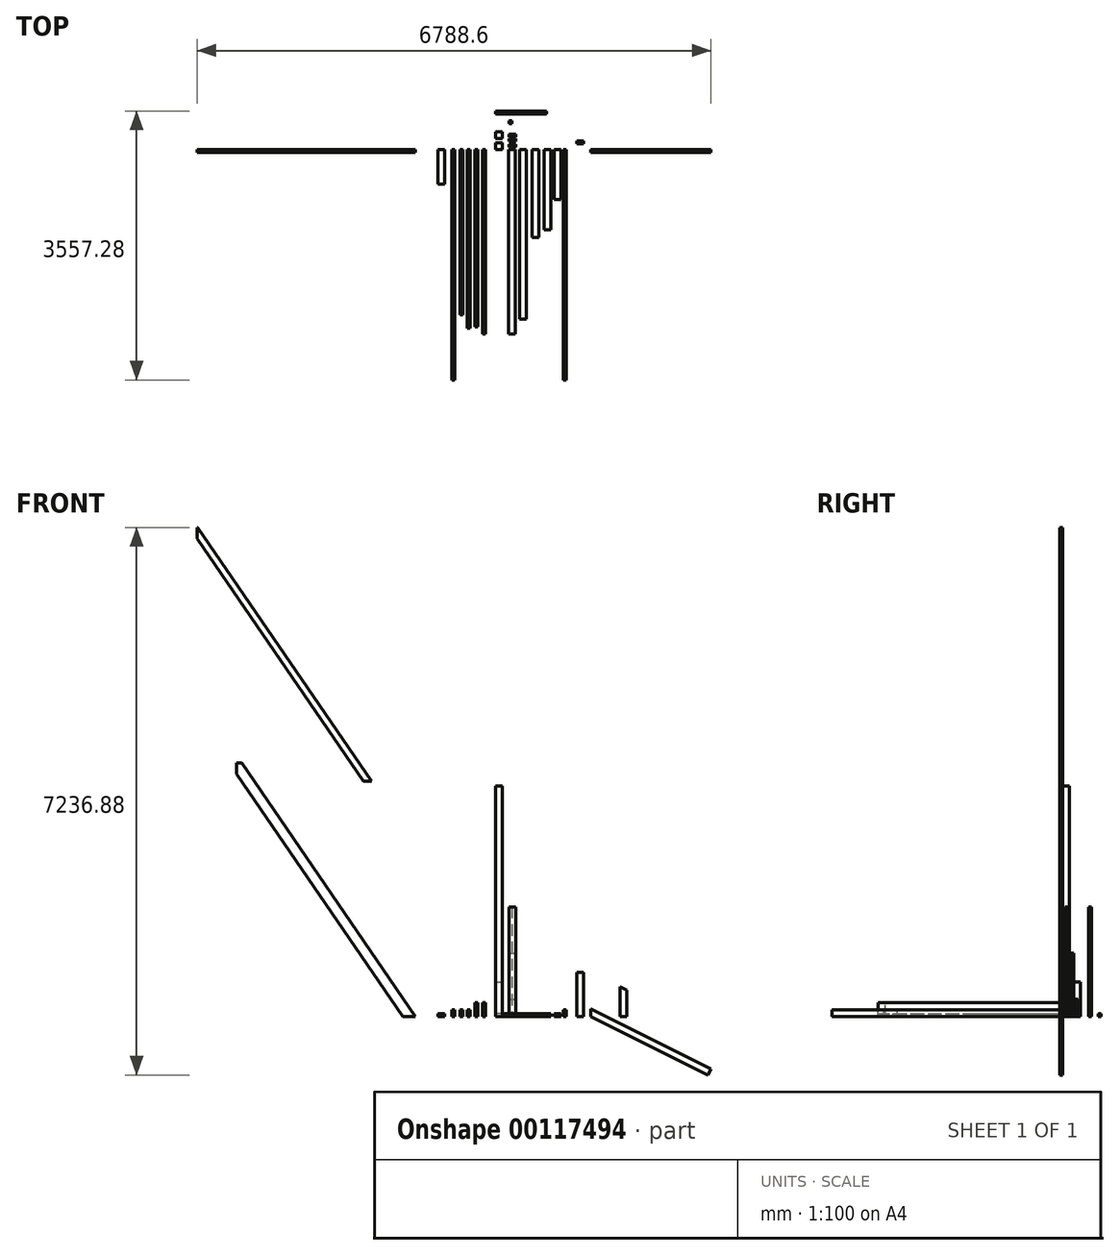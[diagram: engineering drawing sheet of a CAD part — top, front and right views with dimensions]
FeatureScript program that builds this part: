
annotation { "Feature Type Name" : "Feature", "Feature Type Description" : "" }
export const myFeature = defineFeature(function(context is Context, id is Id, definition is map)
    precondition{}
    {
        {
            var Q0;
            Q0=qCreatedBy(makeId("Top.planeOp"),FACE);
            var sketch = newSketch(context, id + "F0", { "sketchPlane" : qUnion([Q0])});
            skLineSegment(sketch, "E0.bottom", {"start": v(0, 0) * mm, "end": v(88.9, 0) * mm});
            skLineSegment(sketch, "E0.top", {"start": v(0, 88.9) * mm, "end": v(88.9, 88.9) * mm});
            skLineSegment(sketch, "E0.left", {"start": v(0, 0) * mm, "end": v(0, 88.9) * mm});
            skLineSegment(sketch, "E0.right", {"start": v(88.9, 0) * mm, "end": v(88.9, 88.9) * mm});
            skSolve(sketch);
        }
        {
            var Q0;
            Q0=makeQuery(id+"F0.imprint","IMPRINT",FACE,{"disambiguationData":[TD([[makeQuery(id+"F0.imprint","IMPRINT",EDGE,{"derivedFrom":sQuery(id+"F0.wireOp",EDGE,"E0.bottom")}),1.0]])]});
            extrude(context, id + "F1", {"entities" : qUnion([Q0]), "depth" : 3048 * mm});
        }
        {
            var Q0;
            Q0=qCreatedBy(makeId("Front.planeOp"),FACE);
            var sketch = newSketch(context, id + "F2", { "sketchPlane" : qUnion([Q0])});
            skLineSegment(sketch, "E1.bottom", {"start": v(-133.1, 0) * mm, "end": v(-171.2, 0) * mm});
            skLineSegment(sketch, "E1.top", {"start": v(-133.1, 184.15) * mm, "end": v(-171.2, 184.15) * mm});
            skLineSegment(sketch, "E1.left", {"start": v(-133.1, 0) * mm, "end": v(-133.1, 184.15) * mm});
            skLineSegment(sketch, "E1.right", {"start": v(-171.2, 0) * mm, "end": v(-171.2, 184.15) * mm});
            skSolve(sketch);
        }
        {
            var Q0;
            Q0=makeQuery(id+"F2.imprint","IMPRINT",FACE,{"disambiguationData":[TD([[makeQuery(id+"F2.imprint","IMPRINT",EDGE,{"derivedFrom":sQuery(id+"F2.wireOp",EDGE,"E1.bottom")}),-1.0]])]});
            extrude(context, id + "F3", {"entities" : qUnion([Q0]), "depth" : 2438.4 * mm});
        }
        {
            var Q0;
            Q0=qCreatedBy(makeId("Front.planeOp"),FACE);
            var sketch = newSketch(context, id + "F4", { "sketchPlane" : qUnion([Q0])});
            skLineSegment(sketch, "E2.bottom", {"start": v(-232.89, 0.98) * mm, "end": v(-270.99, 0.98) * mm});
            skLineSegment(sketch, "E2.top", {"start": v(-232.89, 185.13) * mm, "end": v(-270.99, 185.13) * mm});
            skLineSegment(sketch, "E2.left", {"start": v(-232.89, 0.98) * mm, "end": v(-232.89, 185.13) * mm});
            skLineSegment(sketch, "E2.right", {"start": v(-270.99, 0.98) * mm, "end": v(-270.99, 185.13) * mm});
            skSolve(sketch);
        }
        {
            var Q0;
            Q0=makeQuery(id+"F4.imprint","IMPRINT",FACE,{"disambiguationData":[TD([[makeQuery(id+"F4.imprint","IMPRINT",EDGE,{"derivedFrom":sQuery(id+"F4.wireOp",EDGE,"E2.bottom")}),-1.0]])]});
            extrude(context, id + "F5", {"entities" : qUnion([Q0]), "depth" : 2343.15 * mm});
        }
        {
            var Q0;
            Q0=qCreatedBy(makeId("Front.planeOp"),FACE);
            var sketch = newSketch(context, id + "F6", { "sketchPlane" : qUnion([Q0])});
            skLineSegment(sketch, "E3.bottom", {"start": v(-339.8, 0) * mm, "end": v(-377.9, 0) * mm});
            skLineSegment(sketch, "E3.top", {"start": v(-339.8, 88.9) * mm, "end": v(-377.9, 88.9) * mm});
            skLineSegment(sketch, "E3.left", {"start": v(-339.8, 0) * mm, "end": v(-339.8, 88.9) * mm});
            skLineSegment(sketch, "E3.right", {"start": v(-377.9, 0) * mm, "end": v(-377.9, 88.9) * mm});
            skSolve(sketch);
        }
        {
            var Q0;
            Q0=makeQuery(id+"F6.imprint","IMPRINT",FACE,{"disambiguationData":[TD([[makeQuery(id+"F6.imprint","IMPRINT",EDGE,{"derivedFrom":sQuery(id+"F6.wireOp",EDGE,"E3.bottom")}),-1.0]])]});
            extrude(context, id + "F7", {"entities" : qUnion([Q0]), "depth" : 2362.2 * mm});
        }
        {
            var Q0;
            Q0=qCreatedBy(makeId("Front.planeOp"),FACE);
            var sketch = newSketch(context, id + "F8", { "sketchPlane" : qUnion([Q0])});
            skLineSegment(sketch, "E4.bottom", {"start": v(-434.1, 0) * mm, "end": v(-472.2, 0) * mm});
            skLineSegment(sketch, "E4.top", {"start": v(-434.1, 88.9) * mm, "end": v(-472.2, 88.9) * mm});
            skLineSegment(sketch, "E4.left", {"start": v(-434.1, 0) * mm, "end": v(-434.1, 88.9) * mm});
            skLineSegment(sketch, "E4.right", {"start": v(-472.2, 0) * mm, "end": v(-472.2, 88.9) * mm});
            skSolve(sketch);
        }
        {
            var Q0;
            Q0=makeQuery(id+"F8.imprint","IMPRINT",FACE,{"disambiguationData":[TD([[makeQuery(id+"F8.imprint","IMPRINT",EDGE,{"derivedFrom":sQuery(id+"F8.wireOp",EDGE,"E4.bottom")}),-1.0]])]});
            extrude(context, id + "F9", {"entities" : qUnion([Q0]), "depth" : 2184.4 * mm});
        }
        {
            var Q0;
            Q0=qCreatedBy(makeId("Front.planeOp"),FACE);
            var sketch = newSketch(context, id + "F10", { "sketchPlane" : qUnion([Q0])});
            skLineSegment(sketch, "E5.bottom", {"start": v(-537.37, 0) * mm, "end": v(-575.47, 0) * mm});
            skLineSegment(sketch, "E5.top", {"start": v(-537.37, 88.9) * mm, "end": v(-575.47, 88.9) * mm});
            skLineSegment(sketch, "E5.left", {"start": v(-537.37, 0) * mm, "end": v(-537.37, 88.9) * mm});
            skLineSegment(sketch, "E5.right", {"start": v(-575.47, 0) * mm, "end": v(-575.47, 88.9) * mm});
            skSolve(sketch);
        }
        {
            var Q0;
            Q0=makeQuery(id+"F10.imprint","IMPRINT",FACE,{"disambiguationData":[TD([[makeQuery(id+"F10.imprint","IMPRINT",EDGE,{"derivedFrom":sQuery(id+"F10.wireOp",EDGE,"E5.bottom")}),-1.0]])]});
            extrude(context, id + "F11", {"entities" : qUnion([Q0]), "depth" : 3048 * mm});
        }
        {
            var Q0;
            Q0=qCreatedBy(makeId("Front.planeOp"),FACE);
            var sketch = newSketch(context, id + "F12", { "sketchPlane" : qUnion([Q0])});
            skLineSegment(sketch, "E6.bottom", {"start": v(172.1, 0) * mm, "end": v(261, 0) * mm});
            skLineSegment(sketch, "E6.top", {"start": v(172.1, 38.1) * mm, "end": v(261, 38.1) * mm});
            skLineSegment(sketch, "E6.left", {"start": v(172.1, 0) * mm, "end": v(172.1, 38.1) * mm});
            skLineSegment(sketch, "E6.right", {"start": v(261, 0) * mm, "end": v(261, 38.1) * mm});
            skSolve(sketch);
        }
        {
            var Q0;
            Q0=makeQuery(id+"F12.imprint","IMPRINT",FACE,{"disambiguationData":[TD([[makeQuery(id+"F12.imprint","IMPRINT",EDGE,{"derivedFrom":sQuery(id+"F12.wireOp",EDGE,"E6.bottom")}),1.0]])]});
            extrude(context, id + "F13", {"entities" : qUnion([Q0]), "depth" : 2438.4 * mm});
        }
        {
            var Q0;
            Q0=qCreatedBy(makeId("Top.planeOp"),FACE);
            var sketch = newSketch(context, id + "F14", { "sketchPlane" : qUnion([Q0])});
            skLineSegment(sketch, "E7.bottom", {"start": v(174.35, 32.86) * mm, "end": v(263.25, 32.86) * mm});
            skLineSegment(sketch, "E7.top", {"start": v(174.35, 70.96) * mm, "end": v(263.25, 70.96) * mm});
            skLineSegment(sketch, "E7.left", {"start": v(174.35, 32.86) * mm, "end": v(174.35, 70.96) * mm});
            skLineSegment(sketch, "E7.right", {"start": v(263.25, 32.86) * mm, "end": v(263.25, 70.96) * mm});
            skSolve(sketch);
        }
        {
            var Q0;
            Q0=makeQuery(id+"F14.imprint","IMPRINT",FACE,{"disambiguationData":[TD([[makeQuery(id+"F14.imprint","IMPRINT",EDGE,{"derivedFrom":sQuery(id+"F14.wireOp",EDGE,"E7.bottom")}),1.0]])]});
            extrude(context, id + "F15", {"entities" : qUnion([Q0]), "depth" : 1447.8 * mm});
        }
        {
            var Q0;
            Q0=qCreatedBy(makeId("Front.planeOp"),FACE);
            var sketch = newSketch(context, id + "F16", { "sketchPlane" : qUnion([Q0])});
            skLineSegment(sketch, "E8.bottom", {"start": v(314.16, -0.17) * mm, "end": v(403.06, -0.17) * mm});
            skLineSegment(sketch, "E8.top", {"start": v(314.16, 37.93) * mm, "end": v(403.06, 37.93) * mm});
            skLineSegment(sketch, "E8.left", {"start": v(314.16, -0.17) * mm, "end": v(314.16, 37.93) * mm});
            skLineSegment(sketch, "E8.right", {"start": v(403.06, -0.17) * mm, "end": v(403.06, 37.93) * mm});
            skSolve(sketch);
        }
        {
            var Q0;
            Q0=makeQuery(id+"F16.imprint","IMPRINT",FACE,{"disambiguationData":[TD([[makeQuery(id+"F16.imprint","IMPRINT",EDGE,{"derivedFrom":sQuery(id+"F16.wireOp",EDGE,"E8.bottom")}),1.0]])]});
            extrude(context, id + "F17", {"entities" : qUnion([Q0]), "depth" : 2241.55 * mm});
        }
        {
            var Q0;
            Q0=qCreatedBy(makeId("Front.planeOp"),FACE);
            var sketch = newSketch(context, id + "F18", { "sketchPlane" : qUnion([Q0])});
            skLineSegment(sketch, "E9.bottom", {"start": v(483.63, 0) * mm, "end": v(572.53, 0) * mm});
            skLineSegment(sketch, "E9.top", {"start": v(483.63, 38.1) * mm, "end": v(572.53, 38.1) * mm});
            skLineSegment(sketch, "E9.left", {"start": v(483.63, 0) * mm, "end": v(483.63, 38.1) * mm});
            skLineSegment(sketch, "E9.right", {"start": v(572.53, 0) * mm, "end": v(572.53, 38.1) * mm});
            skSolve(sketch);
        }
        {
            var Q0;
            Q0=makeQuery(id+"F18.imprint","IMPRINT",FACE,{"disambiguationData":[TD([[makeQuery(id+"F18.imprint","IMPRINT",EDGE,{"derivedFrom":sQuery(id+"F18.wireOp",EDGE,"E9.bottom")}),1.0]])]});
            extrude(context, id + "F19", {"entities" : qUnion([Q0]), "depth" : 1162.05 * mm});
        }
        {
            var Q0;
            Q0=qCreatedBy(makeId("Front.planeOp"),FACE);
            var sketch = newSketch(context, id + "F20", { "sketchPlane" : qUnion([Q0])});
            skLineSegment(sketch, "E10.bottom", {"start": v(641.92, -0.19) * mm, "end": v(730.82, -0.19) * mm});
            skLineSegment(sketch, "E10.top", {"start": v(641.92, 37.91) * mm, "end": v(730.82, 37.91) * mm});
            skLineSegment(sketch, "E10.left", {"start": v(641.92, -0.19) * mm, "end": v(641.92, 37.91) * mm});
            skLineSegment(sketch, "E10.right", {"start": v(730.82, -0.19) * mm, "end": v(730.82, 37.91) * mm});
            skSolve(sketch);
        }
        {
            var Q0;
            Q0=makeQuery(id+"F20.imprint","IMPRINT",FACE,{"disambiguationData":[TD([[makeQuery(id+"F20.imprint","IMPRINT",EDGE,{"derivedFrom":sQuery(id+"F20.wireOp",EDGE,"E10.bottom")}),1.0]])]});
            extrude(context, id + "F21", {"entities" : qUnion([Q0]), "depth" : 1063.62 * mm});
        }
        {
            var Q0;
            Q0=qCreatedBy(makeId("Top.planeOp"),FACE);
            var sketch = newSketch(context, id + "F22", { "sketchPlane" : qUnion([Q0])});
            skLineSegment(sketch, "E11.bottom", {"start": v(177.69, 104.81) * mm, "end": v(266.59, 104.81) * mm});
            skLineSegment(sketch, "E11.top", {"start": v(177.69, 142.91) * mm, "end": v(266.59, 142.91) * mm});
            skLineSegment(sketch, "E11.left", {"start": v(177.69, 104.81) * mm, "end": v(177.69, 142.91) * mm});
            skLineSegment(sketch, "E11.right", {"start": v(266.59, 104.81) * mm, "end": v(266.59, 142.91) * mm});
            skSolve(sketch);
        }
        {
            var Q0;
            Q0=makeQuery(id+"F22.imprint","IMPRINT",FACE,{"disambiguationData":[TD([[makeQuery(id+"F22.imprint","IMPRINT",EDGE,{"derivedFrom":sQuery(id+"F22.wireOp",EDGE,"E11.bottom")}),1.0]])]});
            extrude(context, id + "F23", {"entities" : qUnion([Q0]), "depth" : 838.2 * mm});
        }
        {
            var Q0;
            Q0=qCreatedBy(makeId("Top.planeOp"),FACE);
            var sketch = newSketch(context, id + "F24", { "sketchPlane" : qUnion([Q0])});
            skLineSegment(sketch, "E12.bottom", {"start": v(175.9, 165.17) * mm, "end": v(264.8, 165.17) * mm});
            skLineSegment(sketch, "E12.top", {"start": v(175.9, 203.27) * mm, "end": v(264.8, 203.27) * mm});
            skLineSegment(sketch, "E12.left", {"start": v(175.9, 165.17) * mm, "end": v(175.9, 203.27) * mm});
            skLineSegment(sketch, "E12.right", {"start": v(264.8, 165.17) * mm, "end": v(264.8, 203.27) * mm});
            skSolve(sketch);
        }
        {
            var Q0;
            Q0=makeQuery(id+"F24.imprint","IMPRINT",FACE,{"disambiguationData":[TD([[makeQuery(id+"F24.imprint","IMPRINT",EDGE,{"derivedFrom":sQuery(id+"F24.wireOp",EDGE,"E12.bottom")}),1.0]])]});
            extrude(context, id + "F25", {"entities" : qUnion([Q0]), "depth" : 228.6 * mm});
        }
        {
            var Q0;
            Q0=qCreatedBy(makeId("Front.planeOp"),FACE);
            var sketch = newSketch(context, id + "F26", { "sketchPlane" : qUnion([Q0])});
            skLineSegment(sketch, "E13.bottom", {"start": v(894.7, 0) * mm, "end": v(932.8, 0) * mm});
            skLineSegment(sketch, "E13.top", {"start": v(894.7, 88.9) * mm, "end": v(932.8, 88.9) * mm});
            skLineSegment(sketch, "E13.left", {"start": v(894.7, 0) * mm, "end": v(894.7, 88.9) * mm});
            skLineSegment(sketch, "E13.right", {"start": v(932.8, 0) * mm, "end": v(932.8, 88.9) * mm});
            skSolve(sketch);
        }
        {
            var Q0;
            Q0=makeQuery(id+"F26.imprint","IMPRINT",FACE,{"disambiguationData":[TD([[makeQuery(id+"F26.imprint","IMPRINT",EDGE,{"derivedFrom":sQuery(id+"F26.wireOp",EDGE,"E13.bottom")}),1.0]])]});
            extrude(context, id + "F27", {"entities" : qUnion([Q0]), "depth" : 3048 * mm});
        }
        {
            var Q0;
            Q0=qCreatedBy(makeId("Front.planeOp"),FACE);
            var sketch = newSketch(context, id + "F28", { "sketchPlane" : qUnion([Q0])});
            skLineSegment(sketch, "E14", {"start": v(1254.29, 0) * mm, "end": v(1254.29, 99.34) * mm});
            skLineSegment(sketch, "E15", {"start": v(1254.29, 99.34) * mm, "end": v(2845.48, -694) * mm});
            skLineSegment(sketch, "E16", {"start": v(2845.48, -694) * mm, "end": v(2805.81, -773.56) * mm});
            skLineSegment(sketch, "E17", {"start": v(2805.81, -773.56) * mm, "end": v(1254.29, 0) * mm});
            skSolve(sketch);
        }
        {
            var Q0;
            Q0=makeQuery(id+"F28.imprint","IMPRINT",FACE,{"disambiguationData":[TD([[makeQuery(id+"F28.imprint","IMPRINT",EDGE,{"derivedFrom":sQuery(id+"F28.wireOp",EDGE,"E14")}),-1.0]])]});
            extrude(context, id + "F29", {"entities" : qUnion([Q0]), "depth" : 38.1 * mm});
        }
        {
            var Q0;
            Q0=qCreatedBy(makeId("Top.planeOp"),FACE);
            var sketch = newSketch(context, id + "F30", { "sketchPlane" : qUnion([Q0])});
            skLineSegment(sketch, "E18.bottom", {"start": v(1070.8, 77.31) * mm, "end": v(1159.7, 77.31) * mm});
            skLineSegment(sketch, "E18.top", {"start": v(1070.8, 115.41) * mm, "end": v(1159.7, 115.41) * mm});
            skLineSegment(sketch, "E18.left", {"start": v(1070.8, 77.31) * mm, "end": v(1070.8, 115.41) * mm});
            skLineSegment(sketch, "E18.right", {"start": v(1159.7, 77.31) * mm, "end": v(1159.7, 115.41) * mm});
            skSolve(sketch);
        }
        {
            var Q0;
            Q0=makeQuery(id+"F30.imprint","IMPRINT",FACE,{"disambiguationData":[TD([[makeQuery(id+"F30.imprint","IMPRINT",EDGE,{"derivedFrom":sQuery(id+"F30.wireOp",EDGE,"E18.bottom")}),1.0]])]});
            extrude(context, id + "F31", {"entities" : qUnion([Q0]), "depth" : 584.2 * mm});
        }
        {
            var Q0;
            Q0=qCreatedBy(makeId("Front.planeOp"),FACE);
            var sketch = newSketch(context, id + "F32", { "sketchPlane" : qUnion([Q0])});
            skLineSegment(sketch, "E19", {"start": v(1644.77, 0) * mm, "end": v(1644.77, 393.7) * mm});
            skLineSegment(sketch, "E20", {"start": v(1644.77, 393.7) * mm, "end": v(1733.67, 349.38) * mm});
            skLineSegment(sketch, "E21", {"start": v(1733.67, 349.38) * mm, "end": v(1733.67, 0) * mm});
            skLineSegment(sketch, "E22", {"start": v(1733.67, 0) * mm, "end": v(1644.77, 0) * mm});
            skSolve(sketch);
        }
        {
            var Q0;
            Q0=makeQuery(id+"F32.imprint","IMPRINT",FACE,{"disambiguationData":[TD([[makeQuery(id+"F32.imprint","IMPRINT",EDGE,{"derivedFrom":sQuery(id+"F32.wireOp",EDGE,"E19")}),-1.0]])]});
            extrude(context, id + "F33", {"entities" : qUnion([Q0]), "depth" : 38.1 * mm});
        }
        {
            var Q0;
            Q0=qCreatedBy(makeId("Top.planeOp"),FACE);
            var sketch = newSketch(context, id + "F34", { "sketchPlane" : qUnion([Q0])});
            skLineSegment(sketch, "E23.bottom", {"start": v(179.33, 343.69) * mm, "end": v(217.43, 343.69) * mm});
            skLineSegment(sketch, "E23.top", {"start": v(179.33, 381.79) * mm, "end": v(217.43, 381.79) * mm});
            skLineSegment(sketch, "E23.left", {"start": v(179.33, 343.69) * mm, "end": v(179.33, 381.79) * mm});
            skLineSegment(sketch, "E23.right", {"start": v(217.43, 343.69) * mm, "end": v(217.43, 381.79) * mm});
            skSolve(sketch);
        }
        {
            var Q0;
            Q0=makeQuery(id+"F34.imprint","IMPRINT",FACE,{"disambiguationData":[TD([[makeQuery(id+"F34.imprint","IMPRINT",EDGE,{"derivedFrom":sQuery(id+"F34.wireOp",EDGE,"E23.bottom")}),1.0]])]});
            extrude(context, id + "F35", {"entities" : qUnion([Q0]), "depth" : 1447.8 * mm});
        }
        {
            var Q0;
            Q0=qCreatedBy(makeId("Right.planeOp"),FACE);
            var sketch = newSketch(context, id + "F36", { "sketchPlane" : qUnion([Q0])});
            skLineSegment(sketch, "E24.bottom", {"start": v(471.18, 0) * mm, "end": v(509.28, 0) * mm});
            skLineSegment(sketch, "E24.top", {"start": v(471.18, 38.1) * mm, "end": v(509.28, 38.1) * mm});
            skLineSegment(sketch, "E24.left", {"start": v(471.18, 0) * mm, "end": v(471.18, 38.1) * mm});
            skLineSegment(sketch, "E24.right", {"start": v(509.28, 0) * mm, "end": v(509.28, 38.1) * mm});
            skSolve(sketch);
        }
        {
            var Q0;
            Q0=makeQuery(id+"F36.imprint","IMPRINT",FACE,{"disambiguationData":[TD([[makeQuery(id+"F36.imprint","IMPRINT",EDGE,{"derivedFrom":sQuery(id+"F36.wireOp",EDGE,"E24.bottom")}),1.0]])]});
            extrude(context, id + "F37", {"entities" : qUnion([Q0]), "depth" : 673.1 * mm});
        }
        {
            var Q0;
            Q0=qCreatedBy(makeId("Front.planeOp"),FACE);
            var sketch = newSketch(context, id + "F38", { "sketchPlane" : qUnion([Q0])});
            skLineSegment(sketch, "E25.bottom", {"start": v(774.03, 0) * mm, "end": v(862.93, 0) * mm});
            skLineSegment(sketch, "E25.top", {"start": v(774.03, 38.1) * mm, "end": v(862.93, 38.1) * mm});
            skLineSegment(sketch, "E25.left", {"start": v(774.03, 0) * mm, "end": v(774.03, 38.1) * mm});
            skLineSegment(sketch, "E25.right", {"start": v(862.93, 0) * mm, "end": v(862.93, 38.1) * mm});
            skSolve(sketch);
        }
        {
            var Q0;
            Q0=makeQuery(id+"F38.imprint","IMPRINT",FACE,{"disambiguationData":[TD([[makeQuery(id+"F38.imprint","IMPRINT",EDGE,{"derivedFrom":sQuery(id+"F38.wireOp",EDGE,"E25.bottom")}),1.0]])]});
            extrude(context, id + "F39", {"entities" : qUnion([Q0]), "depth" : 663.57 * mm});
        }
        {
            var Q0;
            Q0=qCreatedBy(makeId("Front.planeOp"),FACE);
            var sketch = newSketch(context, id + "F40", { "sketchPlane" : qUnion([Q0])});
            skLineSegment(sketch, "E26", {"start": v(-1059.15, 0) * mm, "end": v(-3355.85, 3352.8) * mm});
            skLineSegment(sketch, "E27", {"start": v(-3355.85, 3352.8) * mm, "end": v(-3424.7, 3352.8) * mm});
            skLineSegment(sketch, "E28", {"start": v(-3424.7, 3352.8) * mm, "end": v(-3424.7, 3206.12) * mm});
            skLineSegment(sketch, "E29", {"start": v(-3424.7, 3206.12) * mm, "end": v(-1228.48, 0) * mm});
            skLineSegment(sketch, "E30", {"start": v(-1228.48, 0) * mm, "end": v(-1059.15, 0) * mm});
            skSolve(sketch);
        }
        {
            var Q0;
            Q0=makeQuery(id+"F40.imprint","IMPRINT",FACE,{"disambiguationData":[TD([[makeQuery(id+"F40.imprint","IMPRINT",EDGE,{"derivedFrom":sQuery(id+"F40.wireOp",EDGE,"E26")}),1.0]])]});
            extrude(context, id + "F41", {"entities" : qUnion([Q0]), "depth" : 38.1 * mm});
        }
        {
            var Q0;
            Q0=qCreatedBy(makeId("Top.planeOp"),FACE);
            var sketch = newSketch(context, id + "F42", { "sketchPlane" : qUnion([Q0])});
            skLineSegment(sketch, "E31.bottom", {"start": v(0, 147.19) * mm, "end": v(88.9, 147.19) * mm});
            skLineSegment(sketch, "E31.top", {"start": v(0, 236.09) * mm, "end": v(88.9, 236.09) * mm});
            skLineSegment(sketch, "E31.left", {"start": v(0, 147.19) * mm, "end": v(0, 236.09) * mm});
            skLineSegment(sketch, "E31.right", {"start": v(88.9, 147.19) * mm, "end": v(88.9, 236.09) * mm});
            skSolve(sketch);
        }
        {
            var Q0;
            Q0=makeQuery(id+"F42.imprint","IMPRINT",FACE,{"disambiguationData":[TD([[makeQuery(id+"F42.imprint","IMPRINT",EDGE,{"derivedFrom":sQuery(id+"F42.wireOp",EDGE,"E31.bottom")}),1.0]])]});
            extrude(context, id + "F43", {"entities" : qUnion([Q0]), "depth" : 457.2 * mm});
        }
        {
            var Q0;
            Q0=qCreatedBy(makeId("Front.planeOp"),FACE);
            var sketch = newSketch(context, id + "F44", { "sketchPlane" : qUnion([Q0])});
            skLineSegment(sketch, "E32.bottom", {"start": v(-671.74, 0) * mm, "end": v(-760.64, 0) * mm});
            skLineSegment(sketch, "E32.top", {"start": v(-671.74, 38.1) * mm, "end": v(-760.64, 38.1) * mm});
            skLineSegment(sketch, "E32.left", {"start": v(-671.74, 0) * mm, "end": v(-671.74, 38.1) * mm});
            skLineSegment(sketch, "E32.right", {"start": v(-760.64, 0) * mm, "end": v(-760.64, 38.1) * mm});
            skSolve(sketch);
        }
        {
            var Q0;
            Q0=makeQuery(id+"F44.imprint","IMPRINT",FACE,{"disambiguationData":[TD([[makeQuery(id+"F44.imprint","IMPRINT",EDGE,{"derivedFrom":sQuery(id+"F44.wireOp",EDGE,"E32.bottom")}),-1.0]])]});
            extrude(context, id + "F45", {"entities" : qUnion([Q0]), "depth" : 457.2 * mm});
        }
        {
            var Q0;
            Q0=qCreatedBy(makeId("Front.planeOp"),FACE);
            var sketch = newSketch(context, id + "F46", { "sketchPlane" : qUnion([Q0])});
            skLineSegment(sketch, "E33", {"start": v(-1639.14, 3110.52) * mm, "end": v(-3935.84, 6463.32) * mm});
            skLineSegment(sketch, "E34", {"start": v(-3935.84, 6463.32) * mm, "end": v(-3943.12, 6463.32) * mm});
            skLineSegment(sketch, "E35", {"start": v(-3943.12, 6463.32) * mm, "end": v(-3943.12, 6316.63) * mm});
            skLineSegment(sketch, "E36", {"start": v(-3943.12, 6316.63) * mm, "end": v(-1746.9, 3110.52) * mm});
            skLineSegment(sketch, "E37", {"start": v(-1746.9, 3110.52) * mm, "end": v(-1639.14, 3110.52) * mm});
            skSolve(sketch);
        }
        {
            var Q0;
            Q0=makeQuery(id+"F46.imprint","IMPRINT",FACE,{"disambiguationData":[TD([[makeQuery(id+"F46.imprint","IMPRINT",EDGE,{"derivedFrom":sQuery(id+"F46.wireOp",EDGE,"E33")}),1.0]])]});
            extrude(context, id + "F47", {"entities" : qUnion([Q0]), "depth" : 38.1 * mm});
        }
    });
